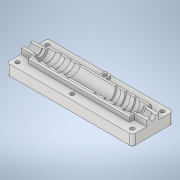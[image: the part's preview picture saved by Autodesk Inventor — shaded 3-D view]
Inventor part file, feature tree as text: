
AUTODESK INVENTOR PART (.ipt)
format: ipt  version: 2021 (Build 250183000, 183)  size: 585,216 bytes
history: native  units: mm
features: sketch x18, extrude x17, projected_geometry x9, fillet x3, other x1, mirror x1, boolean_combine x1, chamfer x1
ambient origin geometry x8: Origin, YZ Plane, XZ Plane, XY Plane, X Axis, Y Axis, Z Axis, Center Point
bodies: Volumenkörper1 (feature_tree), Solid2 (feature_tree), Solid3 (feature_tree)
feature tree (51):
  extrude  "Extrusion1"  Depth=6.0mm
  other  "Spirale1"
  mirror  "Spiegeln1"
  extrude  "Extrusion5"  Depth=4.0mm
  extrude  "Extrusion6"  Depth=1.0mm
  boolean_combine  "Combine1"
  extrude  "Extrusion7"  Depth=10.0mm TaperAngle=0.0deg
  extrude  "Extrusion8"  Depth=100.0mm TaperAngle=0.0deg
  extrude  "Extrusion9"  Depth=24.0mm
  extrude  "Extrusion10"  Depth=12.0mm TaperAngle=0.0deg
  extrude  "Extrusion11"  Depth=16.0mm
  chamfer  "Chamfer2"  Distance=4.0mm
  extrude  "Extrusion12"  Depth=3.0mm
  fillet  "Fillet1"  Radius=3.0mm
  extrude  "Extrusion13"  Depth=4.0mm
  fillet  "Fillet2"  Radius=4.0mm
  extrude  "Extrusion14"  Depth=4.0mm
  extrude  "Extrusion15"  Depth=4.0mm
  extrude  "Extrusion17"  Depth=4.0mm
  extrude  "Extrusion18"  Depth=1.0mm
  extrude  "Extrusion19"  Depth=1.0mm
  extrude  "Extrusion20"  Depth=1.0mm
  extrude  "Extrusion21"  Depth=6.0mm
  fillet  "Fillet3"  Radius=10.0mm
  sketch  "Skizze1"  dims[d0=6.0mm d1=11.0mm]
  sketch  "Skizze3"  dims[d2=36.0mm d3=0.0mm]
  projected_geometry  "Projizierte Kontur2"
  sketch  "Sketch7"  dims[d8=7.0mm d9=24.5mm d10=10.0mm d11=0.0mm d12=90.0deg d13=90.0deg d14=0.0mm d15=0.0mm d16=4.0mm]
  sketch  "Sketch8"  dims[d17=13.962634mm d18=1.0mm]
  sketch  "Sketch9"  dims[d19=0.1mm d32=10.0mm d33=0.0mm]
  projected_geometry  "Projected Loop4"
  sketch  "Sketch10"  dims[d34=7.0mm d35=100.0mm d36=0.0mm]
  projected_geometry  "Projected Loop5"
  projected_geometry  "Projected Loop6"
  projected_geometry  "Projected Loop7"
  projected_geometry  "Projected Loop8"
  sketch  "Sketch11"  dims[d37=82.0mm d38=0.0mm d39=24.0mm]
  projected_geometry  "Projected Loop9"
  sketch  "Sketch12"  dims[d40=30.0mm d41=12.0mm d42=0.0mm]
  sketch  "Sketch13"  dims[d43=74.0mm d44=16.0mm]
  projected_geometry  "Projected Loop10"
  projected_geometry  "Projected Loop11"
  sketch  "Sketch14"  dims[d45=79.0mm]
  sketch  "Sketch15"  dims[d46=21.0mm d47=4.0mm d48=0.0mm]
  sketch  "Sketch16"  dims[d49=3.0mm d50=3.0mm d51=3.0mm]
  sketch  "Sketch17"  dims[d52=3.0mm d53=4.0mm d54=4.0mm]
  sketch  "Sketch19"  dims[d55=4.0mm d56=4.0mm]
  sketch  "Sketch20"  dims[d57=4.0mm d58=4.0mm]
  sketch  "Sketch21"  dims[d59=4.0mm d60=4.0mm]
  sketch  "Sketch22"  dims[d61=10.0mm d62=0.0mm d63=1.0mm]
  sketch  "Sketch23"  dims[d64=1.0mm d65=1.0mm d66=1.0mm d67=6.0mm d68=10.0mm d69=0.0mm d70=10.0mm d71=0.0mm d72=1.0mm d73=2.0mm d74=45.0deg d75=3.0mm d76=3.0mm d77=4.0mm d78=46.0mm d79=4.0mm d80=44.0mm d81=5.5mm d82=5.5mm d83=5.5mm d84=5.5mm d85=5.5mm d86=5.5mm d87=5.0mm d88=0.0mm d89=2.0mm d90=0.5mm d91=6.5mm d92=74.1mm d93=2.1mm d94=0.0mm d95=0.0mm d96=1.0mm d97=12.0mm d98=0.2mm d99=7.9mm d100=0.0mm d101=0.0mm d102=15.0mm d103=0.2mm d104=7.9mm d105=0.0mm d106=0.0mm d109=5.1mm d110=5.0mm d111=0.0mm d112=4.1mm d113=3.1mm d114=0.0mm d115=0.2mm d116=0.0mm d117=5.1mm d118=7.9mm d119=0.0mm d120=5.0mm d121=5.0mm d122=2.0mm d123=0.0mm d124=1.0mm]
